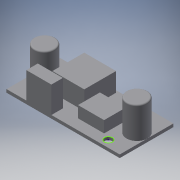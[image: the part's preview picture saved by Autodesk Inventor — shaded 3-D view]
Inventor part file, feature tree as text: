
AUTODESK INVENTOR PART (.ipt)
format: ipt  version: 2016 (Build 200138000, 138)  size: 172,032 bytes
history: native  units: in
note: dims shown in document units (in); Inventor stores cm internally (conversion verified against a paired STEP export)
features: sketch x7, extrude x6, fillet x1
ambient origin geometry x8: Origin, YZ Plane, XZ Plane, XY Plane, X Axis, Y Axis, Z Axis, Center Point
bodies: Solid1 (feature_tree)
feature tree (14):
  extrude  "Extrusion1"  Depth=0.811in
  extrude  "Extrusion2"  Depth=0.315in
  fillet  "Fillet1"  Radius=0.3937in
  extrude  "Extrusion3"  Depth=0.1575in
  extrude  "Extrusion4"  Depth=0.4724in TaperAngle=0.0deg
  extrude  "Extrusion5"  Depth=0.378in
  extrude  "Extrusion6"  TaperAngle=0.0deg  [1 undecoded]
  sketch  "Sketch7"  dims[d15=0.2992in d16=0.3976in d17=0.0in d18=0.1181in d19=0.2795in d20=0.1063in d21=0.1181in d22=0.1063in d23=0.2559in d24=0.3976in d25=0.0in d26=0.4803in d27=0.4803in d28=0.0315in d29=0.3937in d30=0.2835in d31=0.0in d32=0.3937in d33=0.3307in d34=0.1575in d35=0.3937in d36=0.1732in d37=0.0in]
  sketch  "Sketch1"  dims[d0=1.7087in d1=0.811in]
  sketch  "Sketch2"  dims[d2=0.0472in d3=0.0in d4=0.315in d5=0.3937in]
  sketch  "Sketch3"  dims[d6=0.315in d7=0.1575in]
  sketch  "Sketch4"  dims[d8=0.1575in d9=0.4724in d10=0.0in]
  sketch  "Sketch5"  dims[d11=0.0197in d12=0.378in]
  sketch  "Sketch6"  dims[d13=0.1732in d14=0.0in]
note: 1 required parameter value undecoded (feature->parameter linkage not recoverable at this tier; creation-order binding heuristic only, values carry confidence <= 0.55)
